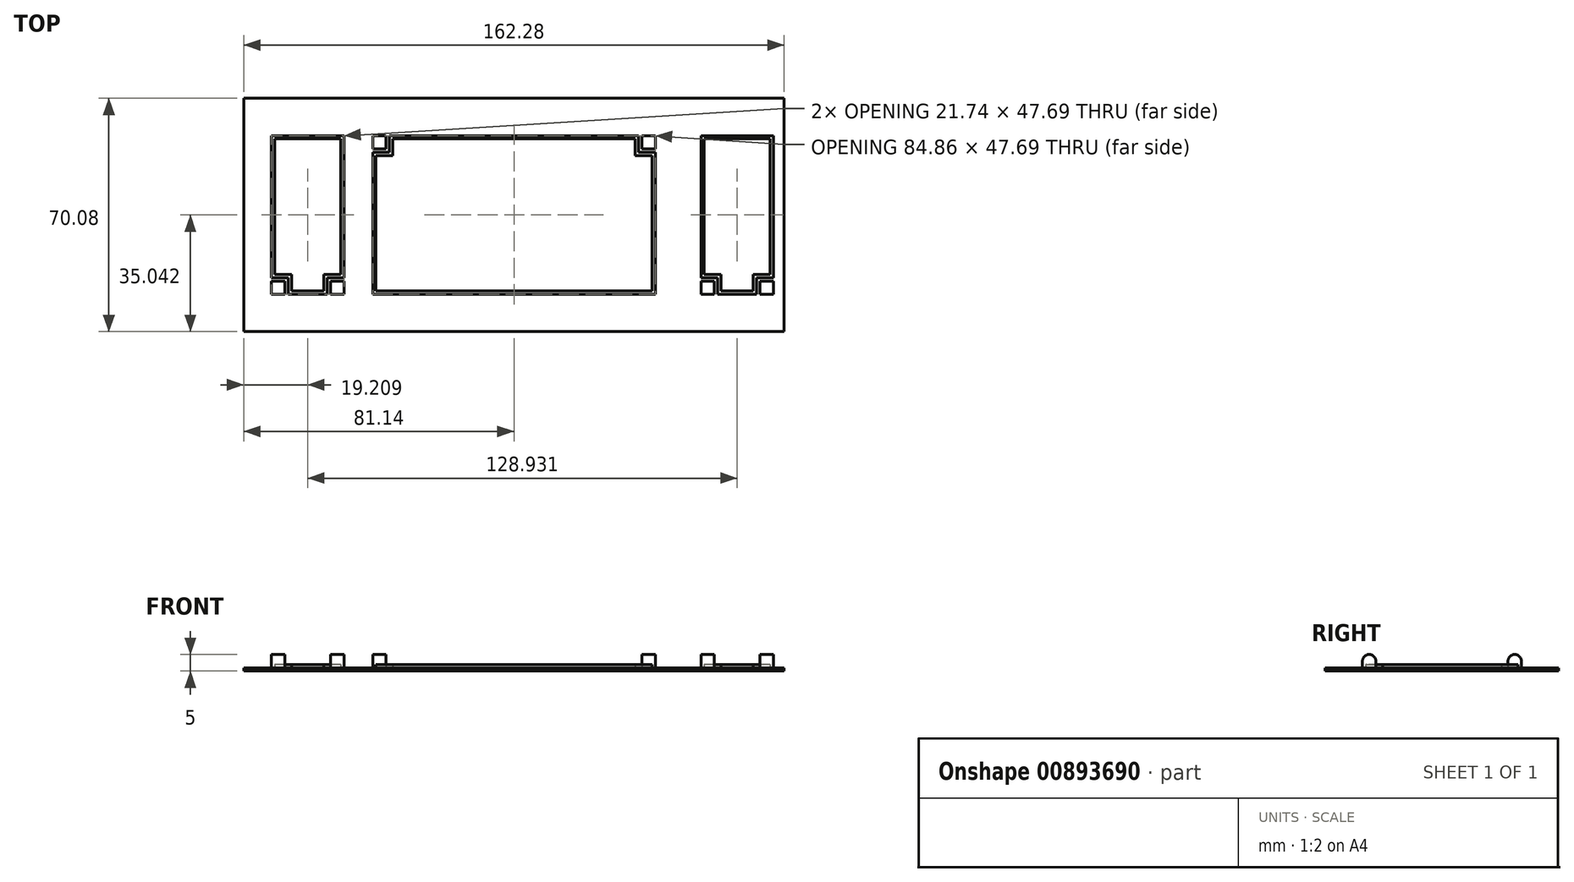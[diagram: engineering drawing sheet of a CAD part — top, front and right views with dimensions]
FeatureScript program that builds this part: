
annotation { "Feature Type Name" : "Feature", "Feature Type Description" : "" }
export const myFeature = defineFeature(function(context is Context, id is Id, definition is map)
    precondition{}
    {
        {
            var Q0;
            Q0=qCreatedBy(makeId("Top.planeOp"),FACE);
            var sketch = newSketch(context, id + "F0", { "sketchPlane" : qUnion([Q0])});
            skLineSegment(sketch, "E0.bottom", {"start": v(-103.56, 47.38) * mm, "end": v(103.56, 47.38) * mm});
            skLineSegment(sketch, "E0.top", {"start": v(-103.56, -43.83) * mm, "end": v(103.56, -43.83) * mm});
            skLineSegment(sketch, "E0.left", {"start": v(-103.56, 47.38) * mm, "end": v(-103.56, -43.83) * mm});
            skLineSegment(sketch, "E0.right", {"start": v(103.56, 47.38) * mm, "end": v(103.56, -43.83) * mm});
            skLineSegment(sketch, "E1.bottom", {"start": v(-81.14, 36.81) * mm, "end": v(81.14, 36.81) * mm});
            skLineSegment(sketch, "E1.top", {"start": v(-81.14, -33.27) * mm, "end": v(81.14, -33.27) * mm});
            skLineSegment(sketch, "E1.left", {"start": v(-81.14, 36.81) * mm, "end": v(-81.14, -33.27) * mm});
            skLineSegment(sketch, "E1.right", {"start": v(81.14, 36.81) * mm, "end": v(81.14, -33.27) * mm});
            skLineSegment(sketch, "E2", {"start": v(-72.8, 25.61) * mm, "end": v(-72.8, -17.07) * mm});
            skLineSegment(sketch, "E3", {"start": v(-67.8, -17.07) * mm, "end": v(-72.8, -17.07) * mm});
            skLineSegment(sketch, "E4", {"start": v(-67.8, -17.07) * mm, "end": v(-67.8, -22.07) * mm});
            skLineSegment(sketch, "E5", {"start": v(72.87, -22.07) * mm, "end": v(72.87, -17.07) * mm});
            skLineSegment(sketch, "E6", {"start": v(77.87, -17.07) * mm, "end": v(72.87, -17.07) * mm});
            skLineSegment(sketch, "E7", {"start": v(77.87, -17.07) * mm, "end": v(77.87, 25.61) * mm});
            skLineSegment(sketch, "E8", {"start": v(77.87, 25.61) * mm, "end": v(56.13, 25.61) * mm});
            skLineSegment(sketch, "E9", {"start": v(56.13, 25.61) * mm, "end": v(56.13, -17.07) * mm});
            skLineSegment(sketch, "E10", {"start": v(61.13, -17.07) * mm, "end": v(56.13, -17.07) * mm});
            skLineSegment(sketch, "E11", {"start": v(61.13, -17.07) * mm, "end": v(61.13, -22.07) * mm});
            skLineSegment(sketch, "E12", {"start": v(61.13, -22.07) * mm, "end": v(72.87, -22.07) * mm});
            skLineSegment(sketch, "E13", {"start": v(-67.8, -22.07) * mm, "end": v(-56.06, -22.07) * mm});
            skLineSegment(sketch, "E14", {"start": v(-56.06, -22.07) * mm, "end": v(-56.06, -17.07) * mm});
            skLineSegment(sketch, "E15", {"start": v(-51.06, -17.07) * mm, "end": v(-56.06, -17.07) * mm});
            skLineSegment(sketch, "E16", {"start": v(-51.06, -17.07) * mm, "end": v(-51.06, 25.61) * mm});
            skLineSegment(sketch, "E17", {"start": v(-51.06, 25.61) * mm, "end": v(-72.8, 25.61) * mm});
            skLineSegment(sketch, "E18", {"start": v(-37.43, 25.61) * mm, "end": v(-37.43, 20.61) * mm});
            skLineSegment(sketch, "E19", {"start": v(-42.43, 20.61) * mm, "end": v(-37.43, 20.61) * mm});
            skLineSegment(sketch, "E20", {"start": v(-42.43, 20.61) * mm, "end": v(-42.43, -22.07) * mm});
            skLineSegment(sketch, "E21", {"start": v(-42.43, -22.07) * mm, "end": v(42.43, -22.07) * mm});
            skLineSegment(sketch, "E22", {"start": v(42.43, -22.07) * mm, "end": v(42.43, 20.61) * mm});
            skLineSegment(sketch, "E23", {"start": v(37.43, 20.61) * mm, "end": v(42.43, 20.61) * mm});
            skLineSegment(sketch, "E24", {"start": v(37.43, 20.61) * mm, "end": v(37.43, 25.61) * mm});
            skLineSegment(sketch, "E25", {"start": v(37.43, 25.61) * mm, "end": v(-37.43, 25.61) * mm});
            skPoint(sketch, "E26", {"position": v(0, 25.61) * mm});
            skPoint(sketch, "E27", {"position": v(0, 47.38) * mm});
            skPoint(sketch, "E28", {"position": v(0, 36.81) * mm});
            skLineSegment(sketch, "E29", {"start": v(0, 25.61) * mm, "end": v(0, 36.81) * mm, "construction": true});
            skLineSegment(sketch, "E30", {"start": v(0, -33.27) * mm, "end": v(0, -22.07) * mm, "construction": true});
            skPoint(sketch, "E31", {"position": v(0, 31.21) * mm});
            skLineSegment(sketch, "E32", {"start": v(0, 36.81) * mm, "end": v(0, 47.38) * mm, "construction": true});
            skLineSegment(sketch, "E33", {"start": v(0, -33.27) * mm, "end": v(0, -43.83) * mm, "construction": true});
            skLineSegment(sketch, "E34.bottom", {"start": v(-72.8, -22.07) * mm, "end": v(-68.8, -22.07) * mm});
            skLineSegment(sketch, "E34.top", {"start": v(-72.8, -18.07) * mm, "end": v(-68.8, -18.07) * mm});
            skLineSegment(sketch, "E34.left", {"start": v(-72.8, -22.07) * mm, "end": v(-72.8, -18.07) * mm});
            skLineSegment(sketch, "E34.right", {"start": v(-68.8, -22.07) * mm, "end": v(-68.8, -18.07) * mm});
            skLineSegment(sketch, "E35.bottom", {"start": v(-51.06, -22.07) * mm, "end": v(-55.06, -22.07) * mm});
            skLineSegment(sketch, "E35.top", {"start": v(-51.06, -18.07) * mm, "end": v(-55.06, -18.07) * mm});
            skLineSegment(sketch, "E35.left", {"start": v(-51.06, -22.07) * mm, "end": v(-51.06, -18.07) * mm});
            skLineSegment(sketch, "E35.right", {"start": v(-55.06, -22.07) * mm, "end": v(-55.06, -18.07) * mm});
            skLineSegment(sketch, "E36.bottom", {"start": v(-42.43, 25.61) * mm, "end": v(-38.43, 25.61) * mm});
            skLineSegment(sketch, "E36.top", {"start": v(-42.43, 21.61) * mm, "end": v(-38.43, 21.61) * mm});
            skLineSegment(sketch, "E36.left", {"start": v(-42.43, 25.61) * mm, "end": v(-42.43, 21.61) * mm});
            skLineSegment(sketch, "E36.right", {"start": v(-38.43, 25.61) * mm, "end": v(-38.43, 21.61) * mm});
            skLineSegment(sketch, "E37.bottom", {"start": v(42.43, 25.61) * mm, "end": v(38.43, 25.61) * mm});
            skLineSegment(sketch, "E37.top", {"start": v(42.43, 21.61) * mm, "end": v(38.43, 21.61) * mm});
            skLineSegment(sketch, "E37.left", {"start": v(42.43, 25.61) * mm, "end": v(42.43, 21.61) * mm});
            skLineSegment(sketch, "E37.right", {"start": v(38.43, 25.61) * mm, "end": v(38.43, 21.61) * mm});
            skLineSegment(sketch, "E38.bottom", {"start": v(56.13, -22.07) * mm, "end": v(60.13, -22.07) * mm});
            skLineSegment(sketch, "E38.top", {"start": v(56.13, -18.07) * mm, "end": v(60.13, -18.07) * mm});
            skLineSegment(sketch, "E38.left", {"start": v(56.13, -22.07) * mm, "end": v(56.13, -18.07) * mm});
            skLineSegment(sketch, "E38.right", {"start": v(60.13, -22.07) * mm, "end": v(60.13, -18.07) * mm});
            skLineSegment(sketch, "E39.bottom", {"start": v(77.87, -22.07) * mm, "end": v(73.87, -22.07) * mm});
            skLineSegment(sketch, "E39.top", {"start": v(77.87, -18.07) * mm, "end": v(73.87, -18.07) * mm});
            skLineSegment(sketch, "E39.left", {"start": v(77.87, -22.07) * mm, "end": v(77.87, -18.07) * mm});
            skLineSegment(sketch, "E39.right", {"start": v(73.87, -22.07) * mm, "end": v(73.87, -18.07) * mm});
            skLineSegment(sketch, "E40.0", {"start": v(-52.06, 24.61) * mm, "end": v(-71.8, 24.61) * mm});
            skLineSegment(sketch, "E40.1", {"start": v(-52.06, -16.07) * mm, "end": v(-52.06, 24.61) * mm});
            skLineSegment(sketch, "E40.2", {"start": v(-71.8, 24.61) * mm, "end": v(-71.8, -16.07) * mm});
            skLineSegment(sketch, "E40.3", {"start": v(-52.06, -16.07) * mm, "end": v(-57.06, -16.07) * mm});
            skLineSegment(sketch, "E40.4", {"start": v(-66.8, -16.07) * mm, "end": v(-71.8, -16.07) * mm});
            skLineSegment(sketch, "E40.5", {"start": v(-66.8, -16.07) * mm, "end": v(-66.8, -21.07) * mm});
            skLineSegment(sketch, "E40.6", {"start": v(-66.8, -21.07) * mm, "end": v(-57.06, -21.07) * mm});
            skLineSegment(sketch, "E40.7", {"start": v(-57.06, -21.07) * mm, "end": v(-57.06, -16.07) * mm});
            skLineSegment(sketch, "E41.0", {"start": v(-41.43, 19.61) * mm, "end": v(-36.43, 19.61) * mm});
            skLineSegment(sketch, "E41.1", {"start": v(-36.43, 24.61) * mm, "end": v(-36.43, 19.61) * mm});
            skLineSegment(sketch, "E41.2", {"start": v(-41.43, 19.61) * mm, "end": v(-41.43, -21.07) * mm});
            skLineSegment(sketch, "E41.3", {"start": v(36.43, 24.61) * mm, "end": v(-36.43, 24.61) * mm});
            skLineSegment(sketch, "E41.4", {"start": v(-41.43, -21.07) * mm, "end": v(41.43, -21.07) * mm});
            skLineSegment(sketch, "E41.5", {"start": v(41.43, -21.07) * mm, "end": v(41.43, 19.61) * mm});
            skLineSegment(sketch, "E41.6", {"start": v(36.43, 19.61) * mm, "end": v(41.43, 19.61) * mm});
            skLineSegment(sketch, "E41.7", {"start": v(36.43, 19.61) * mm, "end": v(36.43, 24.61) * mm});
            skLineSegment(sketch, "E42.0", {"start": v(76.87, 24.61) * mm, "end": v(57.13, 24.61) * mm});
            skLineSegment(sketch, "E42.1", {"start": v(76.87, -16.07) * mm, "end": v(76.87, 24.61) * mm});
            skLineSegment(sketch, "E42.2", {"start": v(57.13, 24.61) * mm, "end": v(57.13, -16.07) * mm});
            skLineSegment(sketch, "E42.3", {"start": v(76.87, -16.07) * mm, "end": v(71.87, -16.07) * mm});
            skLineSegment(sketch, "E42.4", {"start": v(62.13, -16.07) * mm, "end": v(57.13, -16.07) * mm});
            skLineSegment(sketch, "E42.5", {"start": v(62.13, -16.07) * mm, "end": v(62.13, -21.07) * mm});
            skLineSegment(sketch, "E42.6", {"start": v(62.13, -21.07) * mm, "end": v(71.87, -21.07) * mm});
            skLineSegment(sketch, "E42.7", {"start": v(71.87, -21.07) * mm, "end": v(71.87, -16.07) * mm});
            skSolve(sketch);
        }
        {
            var Q0;
            Q0=makeQuery(id+"F0.imprint","IMPRINT",FACE,{"disambiguationData":[TD([[makeQuery(id+"F0.imprint","IMPRINT",EDGE,{"derivedFrom":sQuery(id+"F0.wireOp",EDGE,"E1.bottom")}),-1.0]])]});
            var Q1;
            Q1=makeQuery(id+"F0.imprint","IMPRINT",FACE,{"disambiguationData":[TD([[makeQuery(id+"F0.imprint","IMPRINT",EDGE,{"derivedFrom":sQuery(id+"F0.wireOp",EDGE,"E35.bottom")}),-1.0]])]});
            var Q2;
            Q2=makeQuery(id+"F0.imprint","IMPRINT",FACE,{"disambiguationData":[TD([[makeQuery(id+"F0.imprint","IMPRINT",EDGE,{"derivedFrom":sQuery(id+"F0.wireOp",EDGE,"E34.bottom")}),1.0]])]});
            var Q3;
            Q3=makeQuery(id+"F0.imprint","IMPRINT",FACE,{"disambiguationData":[TD([[makeQuery(id+"F0.imprint","IMPRINT",EDGE,{"derivedFrom":sQuery(id+"F0.wireOp",EDGE,"E37.bottom")}),1.0]])]});
            var Q4;
            Q4=makeQuery(id+"F0.imprint","IMPRINT",FACE,{"disambiguationData":[TD([[makeQuery(id+"F0.imprint","IMPRINT",EDGE,{"derivedFrom":sQuery(id+"F0.wireOp",EDGE,"E36.bottom")}),-1.0]])]});
            var Q5;
            Q5=makeQuery(id+"F0.imprint","IMPRINT",FACE,{"disambiguationData":[TD([[makeQuery(id+"F0.imprint","IMPRINT",EDGE,{"derivedFrom":sQuery(id+"F0.wireOp",EDGE,"E39.bottom")}),-1.0]])]});
            var Q6;
            Q6=makeQuery(id+"F0.imprint","IMPRINT",FACE,{"disambiguationData":[TD([[makeQuery(id+"F0.imprint","IMPRINT",EDGE,{"derivedFrom":sQuery(id+"F0.wireOp",EDGE,"E38.bottom")}),1.0]])]});
            extrude(context, id + "F1", {"entities" : qUnion([Q0, Q1, Q2, Q3, Q4, Q5, Q6]), "oppositeDirection" : true, "depth" : 1 * mm, "offsetDistance" : 25 * mm});
        }
        {
            var Q0;
            Q0=makeQuery(id+"F0.imprint","IMPRINT",FACE,{"disambiguationData":[TD([[makeQuery(id+"F0.imprint","IMPRINT",EDGE,{"derivedFrom":sQuery(id+"F0.wireOp",EDGE,"E34.bottom")}),1.0]])]});
            var Q1;
            Q1=makeQuery(id+"F0.imprint","IMPRINT",FACE,{"disambiguationData":[TD([[makeQuery(id+"F0.imprint","IMPRINT",EDGE,{"derivedFrom":sQuery(id+"F0.wireOp",EDGE,"E35.bottom")}),-1.0]])]});
            var Q2;
            Q2=makeQuery(id+"F0.imprint","IMPRINT",FACE,{"disambiguationData":[TD([[makeQuery(id+"F0.imprint","IMPRINT",EDGE,{"derivedFrom":sQuery(id+"F0.wireOp",EDGE,"E36.bottom")}),-1.0]])]});
            var Q3;
            Q3=makeQuery(id+"F0.imprint","IMPRINT",FACE,{"disambiguationData":[TD([[makeQuery(id+"F0.imprint","IMPRINT",EDGE,{"derivedFrom":sQuery(id+"F0.wireOp",EDGE,"E37.bottom")}),1.0]])]});
            var Q4;
            Q4=makeQuery(id+"F0.imprint","IMPRINT",FACE,{"disambiguationData":[TD([[makeQuery(id+"F0.imprint","IMPRINT",EDGE,{"derivedFrom":sQuery(id+"F0.wireOp",EDGE,"E39.bottom")}),-1.0]])]});
            var Q5;
            Q5=makeQuery(id+"F0.imprint","IMPRINT",FACE,{"disambiguationData":[TD([[makeQuery(id+"F0.imprint","IMPRINT",EDGE,{"derivedFrom":sQuery(id+"F0.wireOp",EDGE,"E38.bottom")}),1.0]])]});
            extrude(context, id + "F2", {"entities" : qUnion([Q0, Q1, Q2, Q3, Q4, Q5]), "operationType" : NewBodyOperationType.ADD, "depth" : 4 * mm, "offsetDistance" : 25 * mm});
        }
        {
            var Q0;
            Q0=makeQuery(id+"F2.opExtrude","CAP_EDGE",EDGE,{"disambiguationData":[OSD([sQuery(id+"F0.wireOp",EDGE,"E34.top")])],"isStart":false});
            var Q1;
            Q1=makeQuery(id+"F2.opExtrude","CAP_EDGE",EDGE,{"disambiguationData":[OSD([sQuery(id+"F0.wireOp",EDGE,"E34.bottom")])],"isStart":false});
            var Q2;
            Q2=makeQuery(id+"F2.opExtrude","CAP_EDGE",EDGE,{"disambiguationData":[OSD([sQuery(id+"F0.wireOp",EDGE,"E35.top")])],"isStart":false});
            var Q3;
            Q3=makeQuery(id+"F2.opExtrude","CAP_EDGE",EDGE,{"disambiguationData":[OSD([sQuery(id+"F0.wireOp",EDGE,"E35.bottom")])],"isStart":false});
            var Q4;
            Q4=makeQuery(id+"F2.opExtrude","CAP_EDGE",EDGE,{"disambiguationData":[OSD([sQuery(id+"F0.wireOp",EDGE,"E36.bottom")])],"isStart":false});
            var Q5;
            Q5=makeQuery(id+"F2.opExtrude","CAP_EDGE",EDGE,{"disambiguationData":[OSD([sQuery(id+"F0.wireOp",EDGE,"E36.top")])],"isStart":false});
            var Q6;
            Q6=makeQuery(id+"F2.opExtrude","CAP_EDGE",EDGE,{"disambiguationData":[OSD([sQuery(id+"F0.wireOp",EDGE,"E37.bottom")])],"isStart":false});
            var Q7;
            Q7=makeQuery(id+"F2.opExtrude","CAP_EDGE",EDGE,{"disambiguationData":[OSD([sQuery(id+"F0.wireOp",EDGE,"E37.top")])],"isStart":false});
            var Q8;
            Q8=makeQuery(id+"F2.opExtrude","CAP_EDGE",EDGE,{"disambiguationData":[OSD([sQuery(id+"F0.wireOp",EDGE,"E38.top")])],"isStart":false});
            var Q9;
            Q9=makeQuery(id+"F2.opExtrude","CAP_EDGE",EDGE,{"disambiguationData":[OSD([sQuery(id+"F0.wireOp",EDGE,"E38.bottom")])],"isStart":false});
            var Q10;
            Q10=makeQuery(id+"F2.opExtrude","CAP_EDGE",EDGE,{"disambiguationData":[OSD([sQuery(id+"F0.wireOp",EDGE,"E39.bottom")])],"isStart":false});
            var Q11;
            Q11=makeQuery(id+"F2.opExtrude","CAP_EDGE",EDGE,{"disambiguationData":[OSD([sQuery(id+"F0.wireOp",EDGE,"E39.top")])],"isStart":false});
            fillet(context, id + "F3", {"entities" : qUnion([Q0, Q1, Q2, Q3, Q4, Q5, Q6, Q7, Q8, Q9, Q10, Q11]), "radius" : 2 * mm, "allowEdgeOverflow" : false});
        }
        {
            var Q0;
            Q0=makeQuery(id+"F0.imprint","IMPRINT",FACE,{"disambiguationData":[TD([[makeQuery(id+"F0.imprint","IMPRINT",EDGE,{"derivedFrom":sQuery(id+"F0.wireOp",EDGE,"E40.0")}),1.0]])]});
            var Q1;
            Q1=makeQuery(id+"F0.imprint","IMPRINT",FACE,{"disambiguationData":[TD([[makeQuery(id+"F0.imprint","IMPRINT",EDGE,{"derivedFrom":sQuery(id+"F0.wireOp",EDGE,"E41.0")}),-1.0]])]});
            var Q2;
            Q2=makeQuery(id+"F0.imprint","IMPRINT",FACE,{"disambiguationData":[TD([[makeQuery(id+"F0.imprint","IMPRINT",EDGE,{"derivedFrom":sQuery(id+"F0.wireOp",EDGE,"E42.0")}),1.0]])]});
            var Q3;
            Q3=makeQuery(id+"F1.opExtrude","CAP_FACE",FACE,{"disambiguationData":[OSD([sQuery(id+"F0.wireOp",EDGE,"E1.bottom"),sQuery(id+"F0.wireOp",EDGE,"E1.top"),sQuery(id+"F0.wireOp",EDGE,"E1.left"),sQuery(id+"F0.wireOp",EDGE,"E1.right"),sQuery(id+"F0.wireOp",EDGE,"E40.0"),sQuery(id+"F0.wireOp",EDGE,"E40.1"),sQuery(id+"F0.wireOp",EDGE,"E40.2"),sQuery(id+"F0.wireOp",EDGE,"E40.3"),sQuery(id+"F0.wireOp",EDGE,"E40.4"),sQuery(id+"F0.wireOp",EDGE,"E40.5"),sQuery(id+"F0.wireOp",EDGE,"E40.6"),sQuery(id+"F0.wireOp",EDGE,"E40.7"),sQuery(id+"F0.wireOp",EDGE,"E41.0"),sQuery(id+"F0.wireOp",EDGE,"E41.1"),sQuery(id+"F0.wireOp",EDGE,"E41.2"),sQuery(id+"F0.wireOp",EDGE,"E41.3"),sQuery(id+"F0.wireOp",EDGE,"E41.4"),sQuery(id+"F0.wireOp",EDGE,"E41.5"),sQuery(id+"F0.wireOp",EDGE,"E41.6"),sQuery(id+"F0.wireOp",EDGE,"E41.7"),sQuery(id+"F0.wireOp",EDGE,"E42.0"),sQuery(id+"F0.wireOp",EDGE,"E42.1"),sQuery(id+"F0.wireOp",EDGE,"E42.2"),sQuery(id+"F0.wireOp",EDGE,"E42.3"),sQuery(id+"F0.wireOp",EDGE,"E42.4"),sQuery(id+"F0.wireOp",EDGE,"E42.5"),sQuery(id+"F0.wireOp",EDGE,"E42.6"),sQuery(id+"F0.wireOp",EDGE,"E42.7")])],"isStart":true});
            extrude(context, id + "F4", {"entities" : qUnion([Q0, Q1, Q2]), "depth" : 1 * mm, "endBoundEntityFace" : qUnion([Q3]), "offsetDistance" : 25 * mm});
        }
    });
